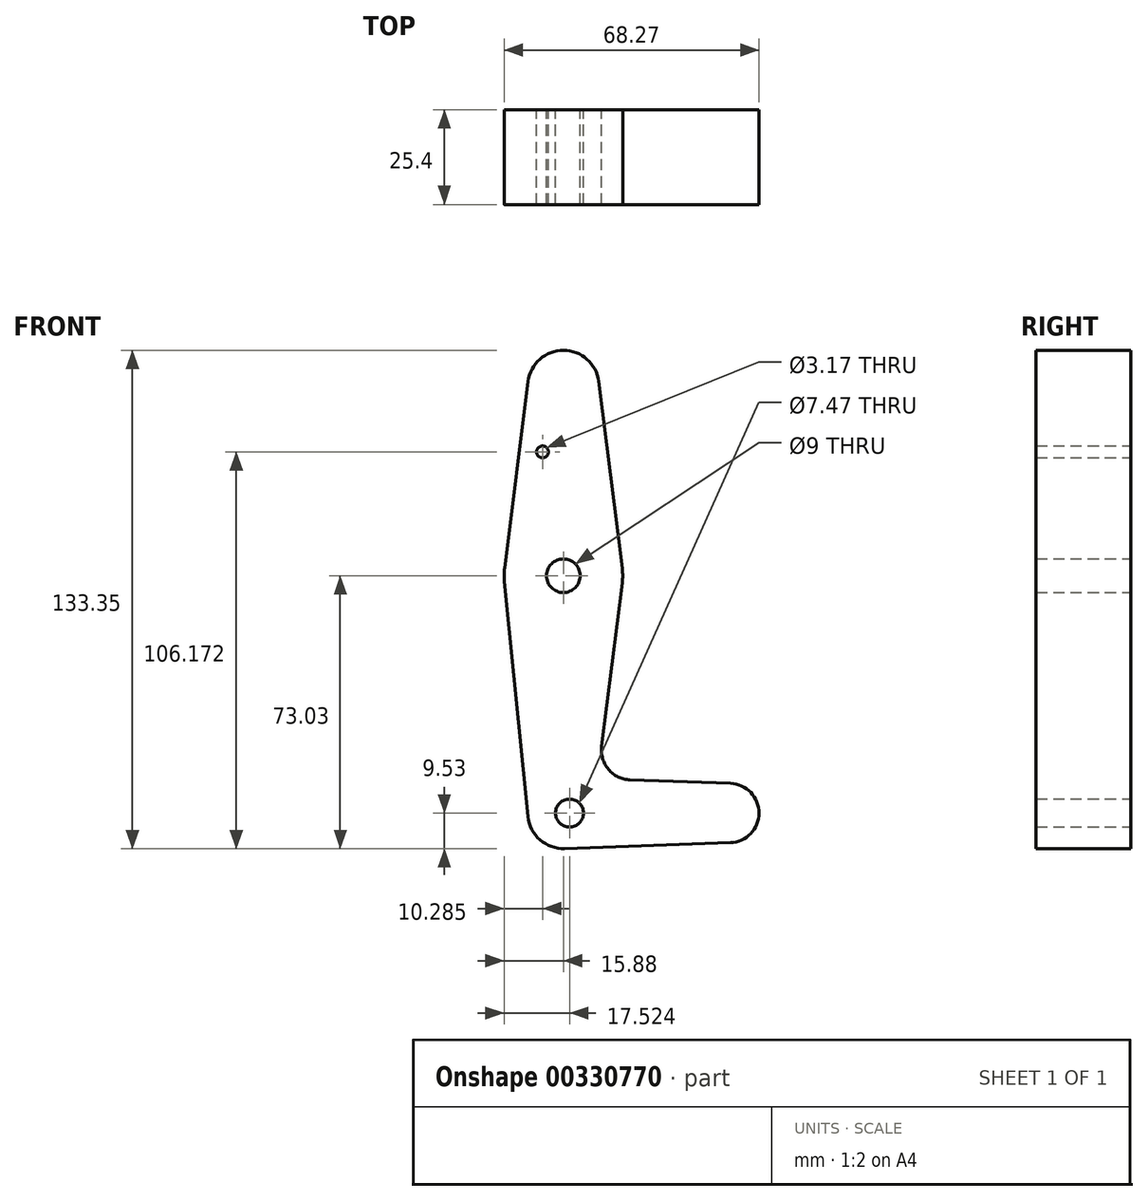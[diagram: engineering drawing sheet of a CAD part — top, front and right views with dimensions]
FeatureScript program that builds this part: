
annotation { "Feature Type Name" : "Feature", "Feature Type Description" : "" }
export const myFeature = defineFeature(function(context is Context, id is Id, definition is map)
    precondition{}
    {
        {
            var Q0;
            Q0=qCreatedBy(makeId("Front.planeOp"),FACE);
            var sketch = newSketch(context, id + "F0", { "sketchPlane" : qUnion([Q0])});
            skLineSegment(sketch, "E0", {"start": v(0, 50.8) * mm, "end": v(0, -63.5) * mm, "construction": true});
            skCircle(sketch, "E1", {"center": v(0, 50.8) * mm, "radius": 9.53 * mm});
            skCircle(sketch, "E2", {"center": v(0, 0) * mm, "radius": 15.88 * mm});
            skCircle(sketch, "E3", {"center": v(0, -63.5) * mm, "radius": 9.53 * mm});
            skLineSegment(sketch, "E4", {"start": v(0, -63.5) * mm, "end": v(44.45, -63.5) * mm, "construction": true});
            skCircle(sketch, "E5", {"center": v(44.45, -63.5) * mm, "radius": 7.94 * mm});
            skLineSegment(sketch, "E6", {"start": v(-9.45, 52) * mm, "end": v(-15.75, 1.98) * mm});
            skLineSegment(sketch, "E7", {"start": v(-15.75, 1.98) * mm, "end": v(-15.75, -1.98) * mm});
            skLineSegment(sketch, "E8", {"start": v(9.45, 52) * mm, "end": v(15.75, 1.98) * mm});
            skLineSegment(sketch, "E9", {"start": v(17.85, -54.6) * mm, "end": v(44.73, -55.57) * mm});
            skLineSegment(sketch, "E10", {"start": v(44.73, -71.43) * mm, "end": v(0.34, -73.02) * mm});
            skLineSegment(sketch, "E11", {"start": v(-15.8, -1.59) * mm, "end": v(-9.48, -64.45) * mm});
            skLineSegment(sketch, "E12", {"start": v(15.75, -1.98) * mm, "end": v(10.25, -45.67) * mm});
            skCircle(sketch, "E13", {"center": v(-5.6, 33.14) * mm, "radius": 1.59 * mm});
            skCircle(sketch, "E14", {"center": v(1.64, -63.5) * mm, "radius": 3.73 * mm});
            skCircle(sketch, "E15", {"center": v(0, 0) * mm, "radius": 4.5 * mm});
            skArc(sketch, "E16.filletArc", {"start": v(10.25, -45.67) * mm, "mid": v(12.08, -51.81) * mm, "end": v(17.85, -54.6) * mm});
            skSolve(sketch);
        }
        {
            var Q0;
            Q0 = qSketchRegion(id + "F0", true);
            extrude(context, id + "F1", {"entities" : qUnion([Q0]), "depth" : 25.4 * mm});
        }
    });
